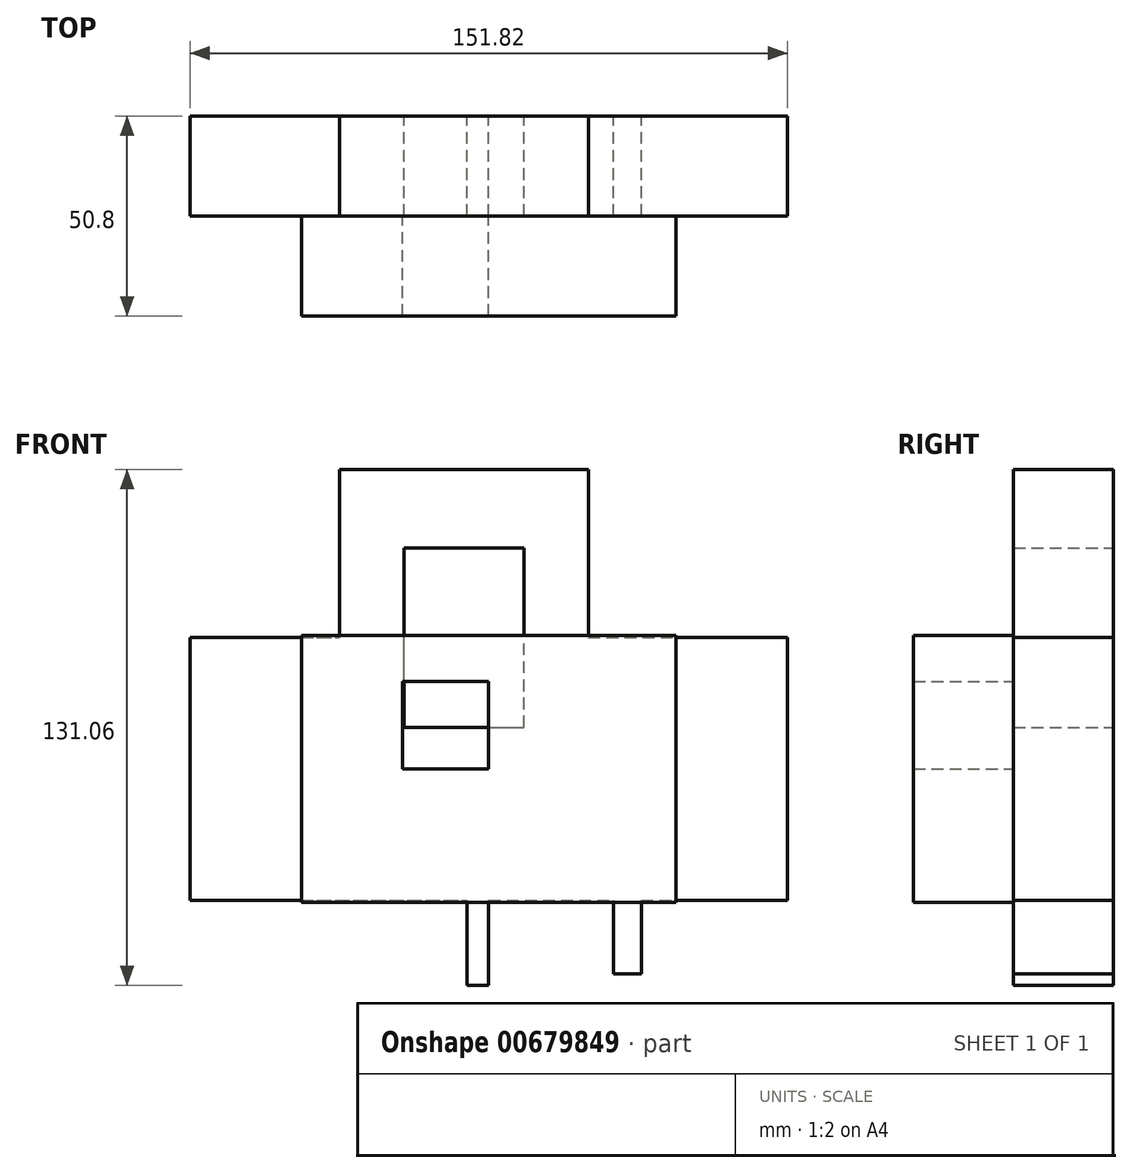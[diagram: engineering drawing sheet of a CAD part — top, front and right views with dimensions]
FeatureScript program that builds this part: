
annotation { "Feature Type Name" : "Feature", "Feature Type Description" : "" }
export const myFeature = defineFeature(function(context is Context, id is Id, definition is map)
    precondition{}
    {
        {
            var Q0;
            Q0=qCreatedBy(makeId("Front.planeOp"),FACE);
            var sketch = newSketch(context, id + "F0", { "sketchPlane" : qUnion([Q0])});
            skLineSegment(sketch, "E0.bottom", {"start": v(-75.91, 33.35) * mm, "end": v(75.91, 33.35) * mm});
            skLineSegment(sketch, "E0.top", {"start": v(-75.91, -33.35) * mm, "end": v(75.91, -33.35) * mm});
            skLineSegment(sketch, "E0.left", {"start": v(-75.91, 33.35) * mm, "end": v(-75.91, -33.35) * mm});
            skLineSegment(sketch, "E0.right", {"start": v(75.91, 33.35) * mm, "end": v(75.91, -33.35) * mm});
            skPoint(sketch, "E0.middle", {"position": v(0, 0) * mm});
            skLineSegment(sketch, "E1.bottom", {"start": v(-37.88, 76.06) * mm, "end": v(25.3, 76.06) * mm});
            skLineSegment(sketch, "E1.top", {"start": v(-37.88, -9.36) * mm, "end": v(25.3, -9.36) * mm});
            skLineSegment(sketch, "E1.left", {"start": v(-37.88, 76.06) * mm, "end": v(-37.88, -9.36) * mm});
            skLineSegment(sketch, "E1.right", {"start": v(25.3, 76.06) * mm, "end": v(25.3, -9.36) * mm});
            skPoint(sketch, "E1.middle", {"position": v(-6.29, 33.35) * mm});
            skLineSegment(sketch, "E2.bottom", {"start": v(-21.5, 10.53) * mm, "end": v(8.92, 10.53) * mm});
            skLineSegment(sketch, "E2.top", {"start": v(-21.5, 56.17) * mm, "end": v(8.92, 56.17) * mm});
            skLineSegment(sketch, "E2.left", {"start": v(-21.5, 10.53) * mm, "end": v(-21.5, 56.17) * mm});
            skLineSegment(sketch, "E2.right", {"start": v(8.92, 10.53) * mm, "end": v(8.92, 56.17) * mm});
            skLineSegment(sketch, "E3.bottom", {"start": v(0, -55) * mm, "end": v(-5.56, -55) * mm});
            skLineSegment(sketch, "E3.top", {"start": v(0, -11.7) * mm, "end": v(-5.56, -11.7) * mm});
            skLineSegment(sketch, "E3.left", {"start": v(0, -55) * mm, "end": v(0, -11.7) * mm});
            skLineSegment(sketch, "E3.right", {"start": v(-5.56, -55) * mm, "end": v(-5.56, -11.7) * mm});
            skPoint(sketch, "E3.middle", {"position": v(-2.78, -33.35) * mm});
            skPoint(sketch, "E3.cornerSnap0", {"position": v(0, -33.35) * mm});
            skLineSegment(sketch, "E4.bottom", {"start": v(38.76, -52.07) * mm, "end": v(31.74, -52.07) * mm});
            skLineSegment(sketch, "E4.top", {"start": v(38.76, 9.95) * mm, "end": v(31.74, 9.95) * mm});
            skLineSegment(sketch, "E4.left", {"start": v(38.76, -52.07) * mm, "end": v(38.76, 9.95) * mm});
            skLineSegment(sketch, "E4.right", {"start": v(31.74, -52.07) * mm, "end": v(31.74, 9.95) * mm});
            skPoint(sketch, "E4.middle", {"position": v(35.25, -21.06) * mm});
            skSolve(sketch);
        }
        {
            var Q0;
            Q0 = qSketchRegion(id + "F0", true);
            extrude(context, id + "F1", {"entities" : qUnion([Q0]), "depth" : 25.4 * mm, "offsetDistance" : 25.4 * mm});
        }
        {
            var Q0;
            Q0=makeQuery(id+"F1.opExtrude","CAP_FACE",FACE,{"disambiguationData":[OSD([sQuery(id+"F0.wireOp",EDGE,"E0.bottom"),sQuery(id+"F0.wireOp",EDGE,"E0.top"),sQuery(id+"F0.wireOp",EDGE,"E0.left"),sQuery(id+"F0.wireOp",EDGE,"E0.right"),sQuery(id+"F0.wireOp",EDGE,"E1.bottom"),sQuery(id+"F0.wireOp",EDGE,"E1.left"),sQuery(id+"F0.wireOp",EDGE,"E1.right"),sQuery(id+"F0.wireOp",EDGE,"E2.bottom"),sQuery(id+"F0.wireOp",EDGE,"E2.top"),sQuery(id+"F0.wireOp",EDGE,"E2.left"),sQuery(id+"F0.wireOp",EDGE,"E2.right"),sQuery(id+"F0.wireOp",EDGE,"E3.bottom"),sQuery(id+"F0.wireOp",EDGE,"E3.left"),sQuery(id+"F0.wireOp",EDGE,"E3.right"),sQuery(id+"F0.wireOp",EDGE,"E4.bottom"),sQuery(id+"F0.wireOp",EDGE,"E4.left"),sQuery(id+"F0.wireOp",EDGE,"E4.right")])],"isStart":false});
            var sketch = newSketch(context, id + "F2", { "sketchPlane" : qUnion([Q0])});
            skSolve(sketch);
        }
        {
            var Q0;
            {var subQ3=sQuery(id+"F0.wireOp",EDGE,"E0.left");Q0=makeQuery(id+"F2.imprint","IMPRINT",FACE,{"disambiguationData":[TD([[makeQuery(id+"F2.imprint","IMPRINT",EDGE,{"derivedFrom":makeQuery(id+"F1.opExtrude","CAP_EDGE",EDGE,{"disambiguationData":[OSD([subQ3])],"isStart":false})}),1.0]])]});}
            var sketch = newSketch(context, id + "F3", { "sketchPlane" : qUnion([Q0])});
            skLineSegment(sketch, "E5.bottom", {"start": v(0, 0) * mm, "end": v(-21.94, 0) * mm});
            skLineSegment(sketch, "E5.top", {"start": v(0, 22.23) * mm, "end": v(-21.94, 22.23) * mm});
            skLineSegment(sketch, "E5.left", {"start": v(0, 0) * mm, "end": v(0, 22.23) * mm});
            skLineSegment(sketch, "E5.right", {"start": v(-21.94, 0) * mm, "end": v(-21.94, 22.23) * mm});
            skPoint(sketch, "E5.middle", {"position": v(-10.97, 11.12) * mm});
            skLineSegment(sketch, "E6.bottom", {"start": v(47.54, -33.93) * mm, "end": v(-47.54, -33.93) * mm});
            skLineSegment(sketch, "E6.top", {"start": v(47.54, 33.93) * mm, "end": v(-47.54, 33.93) * mm});
            skLineSegment(sketch, "E6.left", {"start": v(47.54, -33.93) * mm, "end": v(47.54, 33.93) * mm});
            skLineSegment(sketch, "E6.right", {"start": v(-47.54, -33.93) * mm, "end": v(-47.54, 33.93) * mm});
            skPoint(sketch, "E6.middle", {"position": v(0, 0) * mm});
            skSolve(sketch);
        }
        {
            var Q0;
            Q0 = qSketchRegion(id + "F3", true);
            extrude(context, id + "F4", {"entities" : qUnion([Q0]), "operationType" : NewBodyOperationType.ADD, "depth" : 25.4 * mm, "offsetDistance" : 25.4 * mm});
        }
    });
